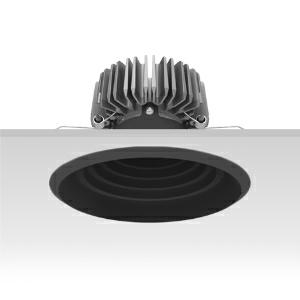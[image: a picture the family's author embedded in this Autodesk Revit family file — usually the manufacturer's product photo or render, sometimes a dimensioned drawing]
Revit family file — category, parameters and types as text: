
# Revit family: 3f_filippi_-_3f_reno_nero_ugr_3f_filippi_-_31642_-_3f_reno_200_bk_3000-840_dali_ugr
name_source: partatom
category: Lighting Fixtures
units: mm (PartAtom-declared; Revit-internal decimal feet)

## family parameters
Cut with Voids When Loaded = No
Host = Face
Light Source = No
Part Type = Normal
Room Calculation Point = No
Round Connector Dimension = Use Diameter
Shared = No

## types (1)
- 3F Filippi - 3F Reno Nero UGR (1 x LED, 3246 lm, 28 W, 4000 K)
    Apparent Load = 28 VA
    Approval mark = CE
    CIE Flux Codes = 91 100 100 100 100
    Color Rendering = 80
    Color Temperature = 4000 K
    Control Gear = Electronic transformer
    Default Elevation = 1800 mm
    Description = ILLUMINOTECHNICAL
Luminous efficiency 100% (DLOR 100%, ULOR 0%).
Initial luminous flux of the luminaire 3246 lm.
Direct symmetric UGR distribution.
Installation Interdistance Transv.D = 0.99 x hu - Long.D = 0.98 x hu.
Average luminance <200 cd/m² for radial angles >65°.
Tabular UGR (CIE 117 - 4H-8H; S=0.25H; 70/50/20): RUG 18.3 - 18.4.
Beam angle: 65° - 64°.
Luminous efficacy 116 lm/W.
Lifetime (L90/B10): 30000 h. (tq+25°C)
Lifetime (L85/B10): 50000 h. (tq+25°C)
Lifetime (L70/B10): 80000 h. (tq+25°C)
Sudden decreased luminous flux after 50000 hours: 0% (C0).
Photobiological safety in compliance with IEC/TR 62778: RG1 low risk, (IEC 62471).
In compliance with IEC/EN 62722-2-1 - IEC/EN 62717 standards.

SOURCE
Compact LED module 3000/840.
Energy efficiency class (UE 2019/2020 - UE 2019/2015): D.
CIE 13.3 Colour rendering index: CRI >80 (R9 <50%).
IES TM-30 Fidelity Index: Rf = 84 Rg = 95.
CCT nominal colour temperature 4000 K.
Colour initial tolerance (MacAdam): SDCM 3.
Zhaga Book 3 compliant.

MECHANICAL
Passive heat dissipator in die-casting aluminium, oversized, for optimum thermal management of the LED module.
Parabolic element with graduated/concentric rings in black polycarbonate.
Internal specular metallic louvre to optimise control of the luminous flux in polycarbonate.
Transparent external lens with glossy and satin differentiated surfaces, with a cooling and anti-insect system in methacrylate (PMMA).
Fastening spring clips in stainless steel.
Dimensions: diameter 216 mm, height 142 mm. Weight 1.52 kg.
IP44 protection degree for exposed part, IP20 for recessed part.
Mechanical strength to impacts IK04 (0.5 joule).
Glow-wire test resistance 650°C.

ELECTRICAL
Wiring on a separate unit.
Halogen Free DALI-2 DATI (Parts 251, 252, 253), PUSH-DIM, electronic wiring 230V-50/60Hz, power factor 0.97 at full load, THD <25%, constant output current, SELV, class II, 1 driver, 1 DALI addresse.
Power of the luminaire 28 W.
ENEC - CE.
SAFE FLICKER: PstLM=<1 and SVM=<0.4 (IEC TR 61547-1 and IEC TR 63158), to ensure a more comfortable and safe light.
Luminaire compliant with EN 60598-2-22 for power supply from a centralised emergency system CPSS (Central Power Supply System), not incorporated in the luminaire - high risk areas excluded. The default power and flux are 100% in AC and 100% in DC.
Ambient temperature from 0°C to +25°C.
Temperature class T6 max 85°C.
Relative humidity UR: <85%.

INSTALLATION
Pull-up recessed fitting.
False ceiling carving: 200 mm.
All accessories dedicated to this product are available on the Catalog and on our website www.3F-Filippi.com.

APPLICATIONS
In environments with VDTs, managerial offices and staterooms, public offices and schools.
In false ceilings with narrow voids.

LIGHT MANAGEMENT
Recommended minimum setting: 10%.
The luminaire, equipped with (DALI-2 DATI) driver, can be controlled manually with 3F Easy Dim technology or automatically/manually with wired or wireless DALI/D2D control systems.
The D2D driver guarantees interoperability with other devices with the same certification by making the following information available:
Device Data (Part 251), Energy Report (Part 252), Diagnosis & Maintenance (Part 253).
In electrical systems without a regulation system (manual or automatic) and DALI bus, a suitable jumper must be made on the DA-DA terminals of the appliance.

WARNING
Luminaire designed for disposal/recycling at end-of-life.
Replaceable (LED only) light source by a professional. Replaceable control gear by a professional.
    Height = 0 mm  [stored 0 ft]
    Lamp = 1 x LED
    Lamp Light Flux = 3246 lm
    Lamp Power = 28 W
    Lamp count = 1
    Length = 216 mm
    Lifetime = 50000 h
    Luminous efficacy = 116 lm/W
    Manufacturer = 3F Filippi
    ModVariant = No
    Model = 3F Filippi - 31642 - 3F Reno 200 BK 3000-840 DALI UGR
    Mounting Place = Ceiling
    Mounting Type = Recessed
    Number of Poles = 1
    OnlyDefault = Yes
    Power Factor = 1
    Product Name = 3F Filippi - 3F Reno Nero UGR
    Product group = recessed luminaire
    ProductGroupID = 4
    Protection Class = Protection class II
    Protection Degree = IP 20
    RLX_Detail_Level = 1
    RLX_Emergency_Light_Flux = 0 lm
    RLX_Emergency_Type = 0
    RLX_Emergency_Type_DB = No
    RlxData = <blob elided: 94669 chars, md5=52517300>
    Socket = socket
    Standby Power = 0 W
    System Light Flux = 3246 lm
    System Power = 28 W
    Type Comments = Product without accessories
    Type Image = 3ffilippi_3f_reno_200_bk_2500_3000_4000.jpg
    URL = http://relux.com
    VarID = ---
    Voltage = 0 V
    Weight = 0.00 kg
    Width = 0 mm  [stored 0 ft]

note: [stored X ft] marks values corroborated as IEEE doubles in the binary element streams (Revit-internal decimal feet)

## geometry (parser evidence)
native form markers: Blend x4, Sweep x9
no freeform markers — native parametric forms only
